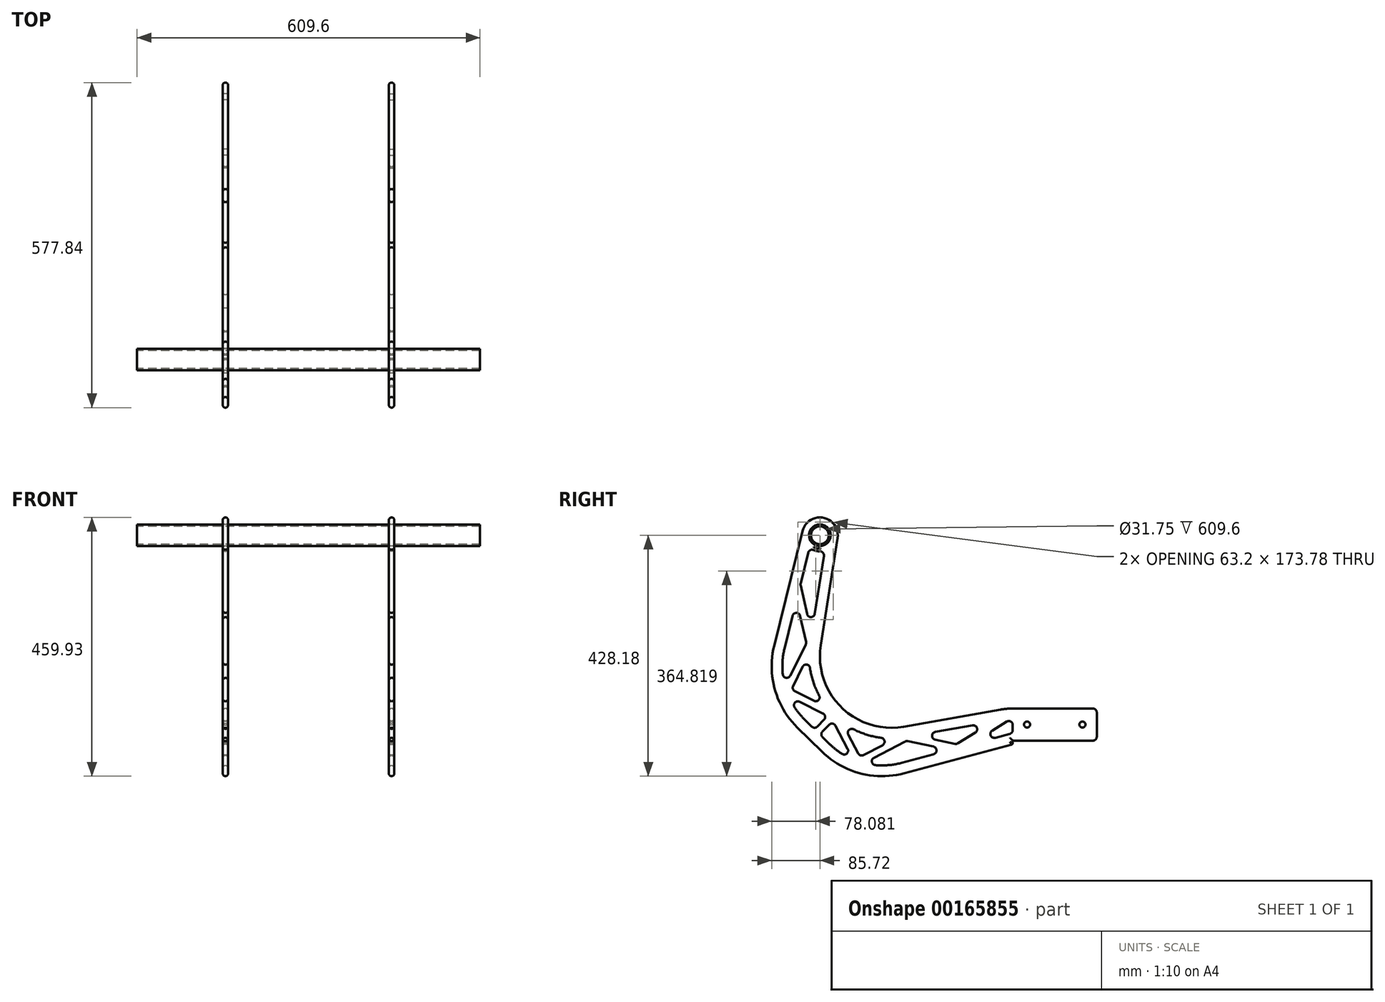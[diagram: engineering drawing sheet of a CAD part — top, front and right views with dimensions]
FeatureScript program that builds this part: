
annotation { "Feature Type Name" : "Feature", "Feature Type Description" : "" }
export const myFeature = defineFeature(function(context is Context, id is Id, definition is map)
    precondition{}
    {
        {
            var Q0;
            Q0=qCreatedBy(makeId("Right.planeOp"),FACE);
            var sketch = newSketch(context, id + "F0", { "sketchPlane" : qUnion([Q0])});
            skLineSegment(sketch, "E0", {"start": v(0, 0) * mm, "end": v(0, -228.6) * mm, "construction": true});
            skLineSegment(sketch, "E1", {"start": v(0, 0) * mm, "end": v(-279.4, 0) * mm, "construction": true});
            skLineSegment(sketch, "E2.bottom", {"start": v(0, 0) * mm, "end": v(149.23, 0) * mm, "construction": true});
            skLineSegment(sketch, "E2.top", {"start": v(0, -3.18) * mm, "end": v(149.23, -3.18) * mm, "construction": true});
            skLineSegment(sketch, "E2.left", {"start": v(0, 0) * mm, "end": v(0, -3.18) * mm, "construction": true});
            skLineSegment(sketch, "E2.right", {"start": v(149.23, 0) * mm, "end": v(149.23, -3.18) * mm, "construction": true});
            skLineSegment(sketch, "E3", {"start": v(-279.4, 0) * mm, "end": v(-279.4, 31.75) * mm, "construction": true});
            skLineSegment(sketch, "E4", {"start": v(-254, 57.15) * mm, "end": v(149.23, 57.15) * mm, "construction": true});
            skLineSegment(sketch, "E5", {"start": v(149.23, 57.15) * mm, "end": v(149.23, 0) * mm, "construction": true});
            skPoint(sketch, "E6.visualSharp", {"position": v(-279.4, 57.15) * mm});
            skArc(sketch, "E6.filletArc", {"start": v(-254, 57.15) * mm, "mid": v(-271.96, 49.71) * mm, "end": v(-279.4, 31.75) * mm, "construction": true});
            skLineSegment(sketch, "E7", {"start": v(-342.9, 0) * mm, "end": v(-342.9, 304.8) * mm, "construction": true});
            skLineSegment(sketch, "E8", {"start": v(-342.9, 0) * mm, "end": v(-279.4, 0) * mm, "construction": true});
            skSolve(sketch);
        }
        {
            var Q0;
            Q0=qCreatedBy(makeId("Right.planeOp"),FACE);
            var sketch = newSketch(context, id + "F1", { "sketchPlane" : qUnion([Q0])});
            skCircle(sketch, "E9", {"center": v(-342.9, 304.8) * mm, "radius": 19.05 * mm});
            skCircle(sketch, "E10", {"center": v(-342.9, 304.8) * mm, "radius": 15.88 * mm});
            skSolve(sketch);
        }
        {
            var Q0;
            Q0 = qSketchRegion(id + "F1", true);
            extrude(context, id + "F2", {"entities" : qUnion([Q0]), "endBound" : BoundingType.SYMMETRIC, "depth" : 609.6 * mm});
        }
        {
            var Q0;
            Q0=qCreatedBy(makeId("Right.planeOp"),FACE);
            cPlane(context, id + "F3", {"entities" : qUnion([Q0]), "cplaneType" : CPlaneType.OFFSET, "offset" : 152.4 * mm, "width" : 152.4 * mm, "height" : 152.4 * mm});
        }
        {
            var Q0;
            Q0=qCreatedBy(id+"F3.planeOp",FACE);
            var sketch = newSketch(context, id + "F4", { "sketchPlane" : qUnion([Q0])});
            skLineSegment(sketch, "E11.0", {"start": v(0, -3.18) * mm, "end": v(149.23, -3.18) * mm});
            skCircle(sketch, "E12", {"center": v(-342.9, 304.8) * mm, "radius": 19.24 * mm});
            skCircle(sketch, "E13", {"center": v(-342.9, 304.8) * mm, "radius": 31.75 * mm, "construction": true});
            skArc(sketch, "E14", {"start": v(-311.53, 299.89) * mm, "mid": v(-336.62, 335.92) * mm, "end": v(-373.72, 312.43) * mm});
            skLineSegment(sketch, "E15", {"start": v(-22.05, -5.1) * mm, "end": v(-193.85, -35.4) * mm});
            skLineSegment(sketch, "E16", {"start": v(-341.37, 109.32) * mm, "end": v(-311.53, 299.89) * mm});
            skLineSegment(sketch, "E17", {"start": v(-373.72, 312.43) * mm, "end": v(-424.16, 108.6) * mm});
            skLineSegment(sketch, "E18", {"start": v(-382.94, -36.8) * mm, "end": v(-339.15, -79.77) * mm});
            skLineSegment(sketch, "E19", {"start": v(-192.98, -118.18) * mm, "end": v(0, -66.47) * mm});
            skLineSegment(sketch, "E20", {"start": v(0, -60.33) * mm, "end": v(149.23, -60.33) * mm});
            skLineSegment(sketch, "E21", {"start": v(149.23, -60.33) * mm, "end": v(149.23, -3.18) * mm});
            skArc(sketch, "E22", {"start": v(-341.37, 109.32) * mm, "mid": v(-304.84, -0.99) * mm, "end": v(-193.85, -35.4) * mm});
            skArc(sketch, "E23", {"start": v(0, -3.18) * mm, "mid": v(-11.07, -3.66) * mm, "end": v(-22.05, -5.1) * mm});
            skLineSegment(sketch, "E24", {"start": v(-422.67, 114.6) * mm, "end": v(-187, -116.58) * mm, "construction": true});
            skLineSegment(sketch, "E25", {"start": v(-361.05, -58.29) * mm, "end": v(-304.84, -0.99) * mm, "construction": true});
            skLineSegment(sketch, "E26", {"start": v(-420.05, 125.18) * mm, "end": v(-381.06, 115.53) * mm, "construction": true});
            skLineSegment(sketch, "E27", {"start": v(-381.06, 115.53) * mm, "end": v(-341.37, 109.32) * mm, "construction": true});
            skLineSegment(sketch, "E28", {"start": v(-420.05, 125.18) * mm, "end": v(-341.37, 109.32) * mm, "construction": true});
            skPoint(sketch, "E29.visualSharp", {"position": v(22.95, -60.33) * mm});
            skPoint(sketch, "E30.visualSharp", {"position": v(-277.03, -140.7) * mm});
            skArc(sketch, "E30.filletArc", {"start": v(-339.15, -79.77) * mm, "mid": v(-271.16, -118.37) * mm, "end": v(-192.98, -118.18) * mm});
            skPoint(sketch, "E31.visualSharp", {"position": v(-445.06, 24.13) * mm});
            skArc(sketch, "E31.filletArc", {"start": v(-424.16, 108.6) * mm, "mid": v(-422.85, 30.43) * mm, "end": v(-382.94, -36.8) * mm});
            skLineSegment(sketch, "E32", {"start": v(0, -60.33) * mm, "end": v(0, -66.47) * mm});
            skSolve(sketch);
        }
        {
            var Q0;
            Q0 = qSketchRegion(id + "F4", true);
            extrude(context, id + "F5", {"entities" : qUnion([Q0]), "oppositeDirection" : true, "depth" : 9.52 * mm});
        }
        {
            var Q0;
            Q0=makeQuery(id+"F5.opExtrude","CAP_FACE",FACE,{"disambiguationData":[OSD([sQuery(id+"F4.wireOp",EDGE,"E11.0"),sQuery(id+"F4.wireOp",EDGE,"E12"),sQuery(id+"F4.wireOp",EDGE,"E14"),sQuery(id+"F4.wireOp",EDGE,"E15"),sQuery(id+"F4.wireOp",EDGE,"E16"),sQuery(id+"F4.wireOp",EDGE,"E17"),sQuery(id+"F4.wireOp",EDGE,"E18"),sQuery(id+"F4.wireOp",EDGE,"E19"),sQuery(id+"F4.wireOp",EDGE,"E20"),sQuery(id+"F4.wireOp",EDGE,"E21"),sQuery(id+"F4.wireOp",EDGE,"E22"),sQuery(id+"F4.wireOp",EDGE,"E23"),sQuery(id+"F4.wireOp",EDGE,"E29.filletArc"),sQuery(id+"F4.wireOp",EDGE,"E30.filletArc"),sQuery(id+"F4.wireOp",EDGE,"E31.filletArc")])],"isStart":true});
            var sketch = newSketch(context, id + "F6", { "sketchPlane" : qUnion([Q0])});
            skArc(sketch, "E33.0", {"start": v(-330.35, 302.84) * mm, "mid": v(-340.39, 317.25) * mm, "end": v(-355.23, 307.85) * mm, "construction": true});
            skLineSegment(sketch, "E33.1", {"start": v(-357.55, 129.11) * mm, "end": v(-335.84, 267.8) * mm});
            skArc(sketch, "E33.2", {"start": v(-361.87, 94.52) * mm, "mid": v(-354.52, 43.68) * mm, "end": v(-330.02, -1.47) * mm});
            skLineSegment(sketch, "E33.5", {"start": v(-369.6, -23.2) * mm, "end": v(-352.24, -40.24) * mm});
            skArc(sketch, "E33.6", {"start": v(-405.67, 104.02) * mm, "mid": v(-409.56, 70.29) * mm, "end": v(-404.8, 36.66) * mm});
            skLineSegment(sketch, "E33.10", {"start": v(-355.23, 307.85) * mm, "end": v(-359.6, 290.15) * mm, "construction": true});
            skLineSegment(sketch, "E34", {"start": v(-347.7, -44.69) * mm, "end": v(-318.18, -14.59) * mm, "construction": true});
            skArc(sketch, "E35", {"start": v(-333.17, 284.82) * mm, "mid": v(-347.3, 283.01) * mm, "end": v(-359.6, 290.15) * mm, "construction": true});
            skLineSegment(sketch, "E36", {"start": v(-333.17, 284.82) * mm, "end": v(-380.97, 203.83) * mm, "construction": true});
            skLineSegment(sketch, "E37", {"start": v(-380.97, 203.83) * mm, "end": v(-360.22, 112.1) * mm, "construction": true});
            skLineSegment(sketch, "E38", {"start": v(-360.22, 112.1) * mm, "end": v(-402.07, 27.9) * mm, "construction": true});
            skLineSegment(sketch, "E39", {"start": v(-402.07, 27.9) * mm, "end": v(-318.18, -14.59) * mm, "construction": true});
            skLineSegment(sketch, "E40.0", {"start": v(-352.24, -40.24) * mm, "end": v(-328.78, -16.33) * mm});
            skLineSegment(sketch, "E40.1", {"start": v(-398.6, 19.02) * mm, "end": v(-328.78, -16.33) * mm});
            skArc(sketch, "E40.2", {"start": v(-345.55, 276.35) * mm, "mid": v(-353.97, 278.46) * mm, "end": v(-361.38, 283) * mm});
            skLineSegment(sketch, "E40.3", {"start": v(-345.55, 276.35) * mm, "end": v(-375.64, 225.34) * mm});
            skLineSegment(sketch, "E40.4", {"start": v(-384.37, 190.09) * mm, "end": v(-366.9, 112.91) * mm});
            skLineSegment(sketch, "E40.5", {"start": v(-366.9, 112.91) * mm, "end": v(-404.8, 36.66) * mm});
            skLineSegment(sketch, "E41.0", {"start": v(-393.58, 30.72) * mm, "end": v(-330.02, -1.47) * mm});
            skLineSegment(sketch, "E41.1", {"start": v(-361.87, 94.52) * mm, "end": v(-393.58, 30.72) * mm});
            skLineSegment(sketch, "E41.2", {"start": v(-374.22, 202.77) * mm, "end": v(-357.55, 129.11) * mm});
            skLineSegment(sketch, "E41.3", {"start": v(-335.84, 267.8) * mm, "end": v(-374.22, 202.77) * mm});
            skLineSegment(sketch, "E42.trimOffspring", {"start": v(-333.17, 284.82) * mm, "end": v(-330.35, 302.84) * mm, "construction": true});
            skArc(sketch, "E43.trimOffspring", {"start": v(-398.6, 19.02) * mm, "mid": v(-386.15, -3.5) * mm, "end": v(-369.6, -23.2) * mm});
            skLineSegment(sketch, "E44", {"start": v(-361.05, -58.29) * mm, "end": v(-347.7, -44.69) * mm, "construction": true});
            skLineSegment(sketch, "E45.trimOffspring", {"start": v(-384.37, 190.09) * mm, "end": v(-405.67, 104.02) * mm});
            skLineSegment(sketch, "E46.trimOffspring", {"start": v(-361.38, 283) * mm, "end": v(-375.64, 225.34) * mm});
            skArc(sketch, "E47.MirrorCS", {"start": v(-26.77, -36.36) * mm, "mid": v(-24.5, -44.75) * mm, "end": v(-19.81, -52.06) * mm});
            skArc(sketch, "E48.MirrorCS", {"start": v(-197.9, -99.78) * mm, "mid": v(-231.56, -104.32) * mm, "end": v(-265.27, -100.22) * mm});
            skLineSegment(sketch, "E49.MirrorCS", {"start": v(-271.43, -89.1) * mm, "end": v(-304.84, -26.17) * mm});
            skArc(sketch, "E50.MirrorCS", {"start": v(-18.54, -23.83) * mm, "mid": v(-20.07, -37.98) * mm, "end": v(-12.7, -50.16) * mm, "construction": true});
            skLineSegment(sketch, "E51.MirrorCS", {"start": v(-112.27, -76.84) * mm, "end": v(-197.9, -99.78) * mm});
            skLineSegment(sketch, "E52.MirrorCS", {"start": v(-173.75, -51.2) * mm, "end": v(-35.5, -26.82) * mm});
            skLineSegment(sketch, "E53.MirrorCS", {"start": v(-189.77, -60.86) * mm, "end": v(-265.27, -100.22) * mm});
            skLineSegment(sketch, "E54.MirrorCS", {"start": v(-19.81, -52.06) * mm, "end": v(-77.19, -67.43) * mm});
            skLineSegment(sketch, "E55.MirrorCS", {"start": v(-26.77, -36.36) * mm, "end": v(-77.19, -67.43) * mm});
            skLineSegment(sketch, "E56.MirrorCS", {"start": v(-35.5, -26.82) * mm, "end": v(-99.78, -66.44) * mm});
            skLineSegment(sketch, "E57.MirrorCS", {"start": v(-208.26, -56.18) * mm, "end": v(-271.43, -89.1) * mm});
            skLineSegment(sketch, "E58.MirrorCS", {"start": v(-274.09, -97.65) * mm, "end": v(-318.18, -14.59) * mm, "construction": true});
            skArc(sketch, "E59.MirrorCS", {"start": v(-208.26, -56.18) * mm, "mid": v(-259.23, -49.8) * mm, "end": v(-304.84, -26.17) * mm});
            skArc(sketch, "E60.MirrorCS", {"start": v(-283.03, -94.35) * mm, "mid": v(-305.78, -82.33) * mm, "end": v(-325.8, -66.17) * mm});
            skLineSegment(sketch, "E61.MirrorCS", {"start": v(-18.54, -23.83) * mm, "end": v(-98.6, -73.17) * mm, "construction": true});
            skLineSegment(sketch, "E62.MirrorCS", {"start": v(-112.27, -76.84) * mm, "end": v(-189.77, -60.86) * mm});
            skLineSegment(sketch, "E63.MirrorCS", {"start": v(-190.7, -54.18) * mm, "end": v(-274.09, -97.65) * mm, "construction": true});
            skLineSegment(sketch, "E64.MirrorCS", {"start": v(-98.6, -73.17) * mm, "end": v(-190.7, -54.18) * mm, "construction": true});
            skLineSegment(sketch, "E65.MirrorCS", {"start": v(-343.17, -49.13) * mm, "end": v(-319.72, -25.23) * mm});
            skLineSegment(sketch, "E66.MirrorCS", {"start": v(-283.03, -94.35) * mm, "end": v(-319.72, -25.23) * mm});
            skLineSegment(sketch, "E67.MirrorCS", {"start": v(-99.78, -66.44) * mm, "end": v(-173.75, -51.2) * mm});
            skLineSegment(sketch, "E68.MirrorCS", {"start": v(-325.8, -66.17) * mm, "end": v(-343.17, -49.13) * mm});
            skLineSegment(sketch, "E69.MirrorCS", {"start": v(4.91, -45.44) * mm, "end": v(-12.7, -50.16) * mm, "construction": true});
            skArc(sketch, "E70.MirrorCS", {"start": v(-0.58, -20.66) * mm, "mid": v(14.02, -30.42) * mm, "end": v(4.91, -45.44) * mm, "construction": true});
            skLineSegment(sketch, "E71.MirrorCS", {"start": v(-18.54, -23.83) * mm, "end": v(-0.58, -20.66) * mm, "construction": true});
            skSolve(sketch);
        }
        {
            var Q0;
            Q0 = qSketchRegion(id + "F6", true);
            extrude(context, id + "F7", {"entities" : qUnion([Q0]), "operationType" : NewBodyOperationType.REMOVE, "oppositeDirection" : true, "depth" : 25.4 * mm});
        }
        {
            var Q0;
            Q0=makeQuery(id+"F5.opExtrude","CAP_FACE",FACE,{"disambiguationData":[OSD([sQuery(id+"F4.wireOp",EDGE,"E11.0"),sQuery(id+"F4.wireOp",EDGE,"E12"),sQuery(id+"F4.wireOp",EDGE,"E14"),sQuery(id+"F4.wireOp",EDGE,"E15"),sQuery(id+"F4.wireOp",EDGE,"E16"),sQuery(id+"F4.wireOp",EDGE,"E17"),sQuery(id+"F4.wireOp",EDGE,"E18"),sQuery(id+"F4.wireOp",EDGE,"E19"),sQuery(id+"F4.wireOp",EDGE,"E20"),sQuery(id+"F4.wireOp",EDGE,"E21"),sQuery(id+"F4.wireOp",EDGE,"E22"),sQuery(id+"F4.wireOp",EDGE,"E23"),sQuery(id+"F4.wireOp",EDGE,"E29.filletArc"),sQuery(id+"F4.wireOp",EDGE,"E30.filletArc"),sQuery(id+"F4.wireOp",EDGE,"E31.filletArc")])],"isStart":true});
            var sketch = newSketch(context, id + "F8", { "sketchPlane" : qUnion([Q0])});
            skLineSegment(sketch, "E72", {"start": v(-377.57, 217.57) * mm, "end": v(-361.38, 283) * mm});
            skArc(sketch, "E73", {"start": v(-361.38, 283) * mm, "mid": v(-348.55, 276.79) * mm, "end": v(-334.31, 277.55) * mm});
            skLineSegment(sketch, "E74", {"start": v(-334.31, 277.55) * mm, "end": v(-357.55, 129.11) * mm});
            skLineSegment(sketch, "E75", {"start": v(-357.55, 129.11) * mm, "end": v(-377.57, 217.57) * mm});
            skLineSegment(sketch, "E76", {"start": v(-77.19, -67.43) * mm, "end": v(0, -19.86) * mm});
            skLineSegment(sketch, "E77", {"start": v(0, -46.75) * mm, "end": v(-77.19, -67.43) * mm});
            skLineSegment(sketch, "E78", {"start": v(0, -19.86) * mm, "end": v(0, -46.75) * mm});
            skSolve(sketch);
        }
        {
            var Q0;
            Q0 = qSketchRegion(id + "F8", true);
            extrude(context, id + "F9", {"entities" : qUnion([Q0]), "operationType" : NewBodyOperationType.REMOVE, "oppositeDirection" : true, "depth" : 25.4 * mm});
        }
        {
            var Q0;
            Q0=makeQuery(id+"F7.boolean.opBoolean","COPY",EDGE,{"derivedFrom":makeQuery(id+"F7.opExtrude","SWEPT_EDGE",EDGE,{"disambiguationData":[OSD([sQuery(id+"F6.wireOp",EDGE,"E33.5"),sQuery(id+"F6.wireOp",EDGE,"E40.0")])]})});
            var Q1;
            Q1=makeQuery(id+"F7.boolean.opBoolean","COPY",EDGE,{"derivedFrom":makeQuery(id+"F7.opExtrude","SWEPT_EDGE",EDGE,{"disambiguationData":[OSD([sQuery(id+"F6.wireOp",EDGE,"E40.0"),sQuery(id+"F6.wireOp",EDGE,"E40.1")])]})});
            var Q2;
            Q2=makeQuery(id+"F7.boolean.opBoolean","COPY",EDGE,{"derivedFrom":makeQuery(id+"F7.opExtrude","SWEPT_EDGE",EDGE,{"disambiguationData":[OSD([sQuery(id+"F6.wireOp",EDGE,"E40.1"),sQuery(id+"F6.wireOp",EDGE,"E43.trimOffspring")])]})});
            var Q3;
            Q3=makeQuery(id+"F7.boolean.opBoolean","COPY",EDGE,{"derivedFrom":makeQuery(id+"F7.opExtrude","SWEPT_EDGE",EDGE,{"disambiguationData":[OSD([sQuery(id+"F6.wireOp",EDGE,"E41.0"),sQuery(id+"F6.wireOp",EDGE,"E41.1")])]})});
            var Q4;
            Q4=makeQuery(id+"F7.boolean.opBoolean","COPY",EDGE,{"derivedFrom":makeQuery(id+"F7.opExtrude","SWEPT_EDGE",EDGE,{"disambiguationData":[OSD([sQuery(id+"F6.wireOp",EDGE,"E33.2"),sQuery(id+"F6.wireOp",EDGE,"E41.0")])]})});
            var Q5;
            Q5=makeQuery(id+"F7.boolean.opBoolean","COPY",EDGE,{"derivedFrom":makeQuery(id+"F7.opExtrude","SWEPT_EDGE",EDGE,{"disambiguationData":[OSD([sQuery(id+"F6.wireOp",EDGE,"E33.2"),sQuery(id+"F6.wireOp",EDGE,"E41.1")])]})});
            var Q6;
            Q6=makeQuery(id+"F7.boolean.opBoolean","COPY",EDGE,{"derivedFrom":makeQuery(id+"F7.opExtrude","SWEPT_EDGE",EDGE,{"disambiguationData":[OSD([sQuery(id+"F6.wireOp",EDGE,"E33.6"),sQuery(id+"F6.wireOp",EDGE,"E40.5")])]})});
            var Q7;
            Q7=makeQuery(id+"F7.boolean.opBoolean","COPY",EDGE,{"derivedFrom":makeQuery(id+"F7.opExtrude","SWEPT_EDGE",EDGE,{"disambiguationData":[OSD([sQuery(id+"F6.wireOp",EDGE,"E40.4"),sQuery(id+"F6.wireOp",EDGE,"E40.5")])]})});
            var Q8;
            Q8=makeQuery(id+"F7.boolean.opBoolean","COPY",EDGE,{"derivedFrom":makeQuery(id+"F7.opExtrude","SWEPT_EDGE",EDGE,{"disambiguationData":[OSD([sQuery(id+"F6.wireOp",EDGE,"E40.4"),sQuery(id+"F6.wireOp",EDGE,"E45.trimOffspring")])]})});
            var Q9;
            Q9=makeQuery(id+"F7.boolean.opBoolean","COPY",EDGE,{"derivedFrom":makeQuery(id+"F7.opExtrude","SWEPT_EDGE",EDGE,{"disambiguationData":[OSD([sQuery(id+"F6.wireOp",EDGE,"E41.2"),sQuery(id+"F6.wireOp",EDGE,"E41.3")])]})});
            var Q10;
            Q10=makeQuery(id+"F7.boolean.opBoolean","COPY",EDGE,{"derivedFrom":makeQuery(id+"F7.opExtrude","SWEPT_EDGE",EDGE,{"disambiguationData":[OSD([sQuery(id+"F6.wireOp",EDGE,"E33.1"),sQuery(id+"F6.wireOp",EDGE,"E41.3")])]})});
            var Q11;
            Q11=makeQuery(id+"F7.boolean.opBoolean","COPY",EDGE,{"derivedFrom":makeQuery(id+"F7.opExtrude","SWEPT_EDGE",EDGE,{"disambiguationData":[OSD([sQuery(id+"F6.wireOp",EDGE,"E33.1"),sQuery(id+"F6.wireOp",EDGE,"E41.2")])]})});
            var Q12;
            Q12=makeQuery(id+"F9.boolean.opBoolean","COPY",EDGE,{"derivedFrom":makeQuery(id+"F9.opExtrude","SWEPT_EDGE",EDGE,{"disambiguationData":[OSD([sQuery(id+"F8.wireOp",EDGE,"E72"),sQuery(id+"F8.wireOp",EDGE,"E75")])]})});
            var Q13;
            Q13=makeQuery(id+"F7.boolean.opBoolean","COPY",EDGE,{"derivedFrom":makeQuery(id+"F7.opExtrude","SWEPT_EDGE",EDGE,{"disambiguationData":[OSD([sQuery(id+"F6.wireOp",EDGE,"E40.2"),sQuery(id+"F6.wireOp",EDGE,"E46.trimOffspring")])]})});
            var Q14;
            Q14=makeQuery(id+"F9.boolean.opBoolean","COPY",EDGE,{"derivedFrom":makeQuery(id+"F9.opExtrude","SWEPT_EDGE",EDGE,{"disambiguationData":[OSD([sQuery(id+"F8.wireOp",EDGE,"E73"),sQuery(id+"F8.wireOp",EDGE,"E74")])]})});
            var Q15;
            Q15=makeQuery(id+"F7.boolean.opBoolean","COPY",EDGE,{"derivedFrom":makeQuery(id+"F7.opExtrude","SWEPT_EDGE",EDGE,{"disambiguationData":[OSD([sQuery(id+"F6.wireOp",EDGE,"E65.MirrorCS"),sQuery(id+"F6.wireOp",EDGE,"E68.MirrorCS")])]})});
            var Q16;
            Q16=makeQuery(id+"F7.boolean.opBoolean","COPY",EDGE,{"derivedFrom":makeQuery(id+"F7.opExtrude","SWEPT_EDGE",EDGE,{"disambiguationData":[OSD([sQuery(id+"F6.wireOp",EDGE,"E65.MirrorCS"),sQuery(id+"F6.wireOp",EDGE,"E66.MirrorCS")])]})});
            var Q17;
            Q17=makeQuery(id+"F7.boolean.opBoolean","COPY",EDGE,{"derivedFrom":makeQuery(id+"F7.opExtrude","SWEPT_EDGE",EDGE,{"disambiguationData":[OSD([sQuery(id+"F6.wireOp",EDGE,"E60.MirrorCS"),sQuery(id+"F6.wireOp",EDGE,"E66.MirrorCS")])]})});
            var Q18;
            Q18=makeQuery(id+"F7.boolean.opBoolean","COPY",EDGE,{"derivedFrom":makeQuery(id+"F7.opExtrude","SWEPT_EDGE",EDGE,{"disambiguationData":[OSD([sQuery(id+"F6.wireOp",EDGE,"E49.MirrorCS"),sQuery(id+"F6.wireOp",EDGE,"E57.MirrorCS")])]})});
            var Q19;
            Q19=makeQuery(id+"F7.boolean.opBoolean","COPY",EDGE,{"derivedFrom":makeQuery(id+"F7.opExtrude","SWEPT_EDGE",EDGE,{"disambiguationData":[OSD([sQuery(id+"F6.wireOp",EDGE,"E49.MirrorCS"),sQuery(id+"F6.wireOp",EDGE,"E59.MirrorCS")])]})});
            var Q20;
            Q20=makeQuery(id+"F7.boolean.opBoolean","COPY",EDGE,{"derivedFrom":makeQuery(id+"F7.opExtrude","SWEPT_EDGE",EDGE,{"disambiguationData":[OSD([sQuery(id+"F6.wireOp",EDGE,"E57.MirrorCS"),sQuery(id+"F6.wireOp",EDGE,"E59.MirrorCS")])]})});
            var Q21;
            Q21=makeQuery(id+"F7.boolean.opBoolean","COPY",EDGE,{"derivedFrom":makeQuery(id+"F7.opExtrude","SWEPT_EDGE",EDGE,{"disambiguationData":[OSD([sQuery(id+"F6.wireOp",EDGE,"E53.MirrorCS"),sQuery(id+"F6.wireOp",EDGE,"E62.MirrorCS")])]})});
            var Q22;
            Q22=makeQuery(id+"F7.boolean.opBoolean","COPY",EDGE,{"derivedFrom":makeQuery(id+"F7.opExtrude","SWEPT_EDGE",EDGE,{"disambiguationData":[OSD([sQuery(id+"F6.wireOp",EDGE,"E48.MirrorCS"),sQuery(id+"F6.wireOp",EDGE,"E53.MirrorCS")])]})});
            var Q23;
            Q23=makeQuery(id+"F7.boolean.opBoolean","COPY",EDGE,{"derivedFrom":makeQuery(id+"F7.opExtrude","SWEPT_EDGE",EDGE,{"disambiguationData":[OSD([sQuery(id+"F6.wireOp",EDGE,"E51.MirrorCS"),sQuery(id+"F6.wireOp",EDGE,"E62.MirrorCS")])]})});
            var Q24;
            Q24=makeQuery(id+"F7.boolean.opBoolean","COPY",EDGE,{"derivedFrom":makeQuery(id+"F7.opExtrude","SWEPT_EDGE",EDGE,{"disambiguationData":[OSD([sQuery(id+"F6.wireOp",EDGE,"E52.MirrorCS"),sQuery(id+"F6.wireOp",EDGE,"E67.MirrorCS")])]})});
            var Q25;
            Q25=makeQuery(id+"F7.boolean.opBoolean","COPY",EDGE,{"derivedFrom":makeQuery(id+"F7.opExtrude","SWEPT_EDGE",EDGE,{"disambiguationData":[OSD([sQuery(id+"F6.wireOp",EDGE,"E56.MirrorCS"),sQuery(id+"F6.wireOp",EDGE,"E67.MirrorCS")])]})});
            var Q26;
            Q26=makeQuery(id+"F7.boolean.opBoolean","COPY",EDGE,{"derivedFrom":makeQuery(id+"F7.opExtrude","SWEPT_EDGE",EDGE,{"disambiguationData":[OSD([sQuery(id+"F6.wireOp",EDGE,"E54.MirrorCS"),sQuery(id+"F6.wireOp",EDGE,"E55.MirrorCS")])]})});
            var Q27;
            Q27=makeQuery(id+"F7.boolean.opBoolean","COPY",EDGE,{"derivedFrom":makeQuery(id+"F7.opExtrude","SWEPT_EDGE",EDGE,{"disambiguationData":[OSD([sQuery(id+"F6.wireOp",EDGE,"E52.MirrorCS"),sQuery(id+"F6.wireOp",EDGE,"E56.MirrorCS")])]})});
            var Q28;
            Q28=makeQuery(id+"F9.boolean.opBoolean","COPY",EDGE,{"derivedFrom":makeQuery(id+"F9.opExtrude","SWEPT_EDGE",EDGE,{"disambiguationData":[OSD([sQuery(id+"F8.wireOp",EDGE,"E76"),sQuery(id+"F8.wireOp",EDGE,"QhLc7K4z-Akcm-oFJL-4TFC-ttLu0XXbbSw1")])]})});
            var Q29;
            Q29=makeQuery(id+"F9.boolean.opBoolean","COPY",EDGE,{"derivedFrom":makeQuery(id+"F9.opExtrude","SWEPT_EDGE",EDGE,{"disambiguationData":[OSD([sQuery(id+"F8.wireOp",EDGE,"QhLc7K4z-Akcm-oFJL-4TFC-ttLu0XXbbSw1"),sQuery(id+"F8.wireOp",EDGE,"bKYI4NnU-ni6z-fiqR-xN9G-CCJAb1qPsRIM")])]})});
            var Q30;
            Q30=makeQuery(id+"F9.boolean.opBoolean","COPY",EDGE,{"derivedFrom":makeQuery(id+"F9.opExtrude","SWEPT_EDGE",EDGE,{"disambiguationData":[OSD([sQuery(id+"F8.wireOp",EDGE,"bKYI4NnU-ni6z-fiqR-xN9G-CCJAb1qPsRIM"),sQuery(id+"F8.wireOp",EDGE,"E77")])]})});
            var Q31;
            Q31=makeQuery(id+"F5.opExtrude","SWEPT_EDGE",EDGE,{"disambiguationData":[OSD([sQuery(id+"F4.wireOp",EDGE,"E11.0"),sQuery(id+"F4.wireOp",EDGE,"E21")])]});
            var Q32;
            Q32=makeQuery(id+"F5.opExtrude","SWEPT_EDGE",EDGE,{"disambiguationData":[OSD([sQuery(id+"F4.wireOp",EDGE,"E20"),sQuery(id+"F4.wireOp",EDGE,"E21")])]});
            fillet(context, id + "F10", {"entities" : qUnion([Q0, Q1, Q2, Q3, Q4, Q5, Q6, Q7, Q8, Q9, Q10, Q11, Q12, Q13, Q14, Q15, Q16, Q17, Q18, Q19, Q20, Q21, Q22, Q23, Q24, Q25, Q26, Q27, Q28, Q29, Q30, Q31, Q32]), "radius" : 7 * mm, "tangentPropagation" : true, "allowEdgeOverflow" : false});
        }
        {
            var Q0;
            Q0=makeQuery(id+"F5.opExtrude","SWEPT_EDGE",EDGE,{"disambiguationData":[OSD([sQuery(id+"F4.wireOp",EDGE,"E19"),sQuery(id+"F4.wireOp",EDGE,"E32")])]});
            fillet(context, id + "F11", {"entities" : qUnion([Q0]), "radius" : 3.17 * mm, "tangentPropagation" : true, "allowEdgeOverflow" : false});
        }
        {
            var Q0;
            Q0=makeQuery(id+"F5.opExtrude","CAP_FACE",FACE,{"disambiguationData":[OSD([sQuery(id+"F4.wireOp",EDGE,"E11.0"),sQuery(id+"F4.wireOp",EDGE,"E12"),sQuery(id+"F4.wireOp",EDGE,"E14"),sQuery(id+"F4.wireOp",EDGE,"E15"),sQuery(id+"F4.wireOp",EDGE,"E16"),sQuery(id+"F4.wireOp",EDGE,"E17"),sQuery(id+"F4.wireOp",EDGE,"E18"),sQuery(id+"F4.wireOp",EDGE,"E19"),sQuery(id+"F4.wireOp",EDGE,"E20"),sQuery(id+"F4.wireOp",EDGE,"E21"),sQuery(id+"F4.wireOp",EDGE,"E22"),sQuery(id+"F4.wireOp",EDGE,"E23"),sQuery(id+"F4.wireOp",EDGE,"E30.filletArc"),sQuery(id+"F4.wireOp",EDGE,"E31.filletArc"),sQuery(id+"F4.wireOp",EDGE,"E32")])],"isStart":true});
            var sketch = newSketch(context, id + "F12", { "sketchPlane" : qUnion([Q0])});
            skLineSegment(sketch, "E79", {"start": v(149.22, -31.75) * mm, "end": v(0, -31.75) * mm, "construction": true});
            skPoint(sketch, "E79.endSnap0", {"position": v(0, -36.88) * mm});
            skLineSegment(sketch, "E80", {"start": v(74.61, -31.75) * mm, "end": v(74.61, -3.18) * mm, "construction": true});
            skPoint(sketch, "E81", {"position": v(123.83, -31.75) * mm});
            skPoint(sketch, "E82.MirrorP", {"position": v(25.4, -31.75) * mm});
            skSolve(sketch);
        }
        {
            var Q0;
            Q0=makeQuery(id+"F5.opExtrude","CAP_FACE",FACE,{"disambiguationData":[OSD([sQuery(id+"F4.wireOp",EDGE,"E11.0"),sQuery(id+"F4.wireOp",EDGE,"E12"),sQuery(id+"F4.wireOp",EDGE,"E14"),sQuery(id+"F4.wireOp",EDGE,"E15"),sQuery(id+"F4.wireOp",EDGE,"E16"),sQuery(id+"F4.wireOp",EDGE,"E17"),sQuery(id+"F4.wireOp",EDGE,"E18"),sQuery(id+"F4.wireOp",EDGE,"E19"),sQuery(id+"F4.wireOp",EDGE,"E20"),sQuery(id+"F4.wireOp",EDGE,"E21"),sQuery(id+"F4.wireOp",EDGE,"E22"),sQuery(id+"F4.wireOp",EDGE,"E23"),sQuery(id+"F4.wireOp",EDGE,"E29.filletArc"),sQuery(id+"F4.wireOp",EDGE,"E30.filletArc"),sQuery(id+"F4.wireOp",EDGE,"E31.filletArc")])],"isStart":true});
            var Q1;
            Q1=makeQuery(id+"F5.opExtrude","CAP_FACE",FACE,{"disambiguationData":[OSD([sQuery(id+"F4.wireOp",EDGE,"E11.0"),sQuery(id+"F4.wireOp",EDGE,"E12"),sQuery(id+"F4.wireOp",EDGE,"E14"),sQuery(id+"F4.wireOp",EDGE,"E15"),sQuery(id+"F4.wireOp",EDGE,"E16"),sQuery(id+"F4.wireOp",EDGE,"E17"),sQuery(id+"F4.wireOp",EDGE,"E18"),sQuery(id+"F4.wireOp",EDGE,"E19"),sQuery(id+"F4.wireOp",EDGE,"E20"),sQuery(id+"F4.wireOp",EDGE,"E21"),sQuery(id+"F4.wireOp",EDGE,"E22"),sQuery(id+"F4.wireOp",EDGE,"E23"),sQuery(id+"F4.wireOp",EDGE,"E29.filletArc"),sQuery(id+"F4.wireOp",EDGE,"E30.filletArc"),sQuery(id+"F4.wireOp",EDGE,"E31.filletArc")])],"isStart":false});
            fillet(context, id + "F13", {"entities" : qUnion([Q0, Q1]), "radius" : 4.76 * mm, "tangentPropagation" : true, "allowEdgeOverflow" : false});
        }
        {
            var Q0;
            Q0=sQuery(id+"F12.wireOp",VERTEX,"E82.MirrorP");
            var Q1;
            Q1=sQuery(id+"F12.wireOp",VERTEX,"E81");
            var Q2;
            Q2=makeQuery(id+"F5.opExtrude","SWEPT_BODY",BODY,{"disambiguationData":[OSD([sQuery(id+"F4.wireOp",EDGE,"E11.0"),sQuery(id+"F4.wireOp",EDGE,"E12"),sQuery(id+"F4.wireOp",EDGE,"E14"),sQuery(id+"F4.wireOp",EDGE,"E15"),sQuery(id+"F4.wireOp",EDGE,"E16"),sQuery(id+"F4.wireOp",EDGE,"E17"),sQuery(id+"F4.wireOp",EDGE,"E18"),sQuery(id+"F4.wireOp",EDGE,"E19"),sQuery(id+"F4.wireOp",EDGE,"E20"),sQuery(id+"F4.wireOp",EDGE,"E21"),sQuery(id+"F4.wireOp",EDGE,"E22"),sQuery(id+"F4.wireOp",EDGE,"E23"),sQuery(id+"F4.wireOp",EDGE,"E30.filletArc"),sQuery(id+"F4.wireOp",EDGE,"E31.filletArc"),sQuery(id+"F4.wireOp",EDGE,"E32")])]});
            hole(context, id + "F14", {"style" : HoleStyle.SIMPLE, "endStyle" : HoleEndStyle.THROUGH, "standardTappedOrClearance" : lookupTablePath({ "standard" : "ANSI", "engagement" : "75%", "pitch" : "13 tpi", "size" : "1/2", "type" : "Tapped" }), "standardBlindInLast" : lookupTablePath({ "standard" : "ANSI", "engagement" : "75%", "pitch" : "13 tpi", "size" : "1/2", "type" : "Tapped" }), "holeDiameter" : 10.72 * mm, "locations" : qUnion([Q0, Q1]), "scope" : qUnion([Q2]), "isTappedThrough" : true, "majorDiameter" : 12.7 * mm, "showTappedDepth" : true});
        }
        {
            var Q0;
            Q0=makeQuery(id+"F5.opExtrude","SWEPT_BODY",BODY,{"disambiguationData":[OSD([sQuery(id+"F4.wireOp",EDGE,"E11.0"),sQuery(id+"F4.wireOp",EDGE,"E12"),sQuery(id+"F4.wireOp",EDGE,"E14"),sQuery(id+"F4.wireOp",EDGE,"E15"),sQuery(id+"F4.wireOp",EDGE,"E16"),sQuery(id+"F4.wireOp",EDGE,"E17"),sQuery(id+"F4.wireOp",EDGE,"E18"),sQuery(id+"F4.wireOp",EDGE,"E19"),sQuery(id+"F4.wireOp",EDGE,"E20"),sQuery(id+"F4.wireOp",EDGE,"E21"),sQuery(id+"F4.wireOp",EDGE,"E22"),sQuery(id+"F4.wireOp",EDGE,"E23"),sQuery(id+"F4.wireOp",EDGE,"E30.filletArc"),sQuery(id+"F4.wireOp",EDGE,"E31.filletArc"),sQuery(id+"F4.wireOp",EDGE,"E32")])]});
            var Q1;
            Q1=qCreatedBy(makeId("Right.planeOp"),FACE);
            mirror(context, id + "F15", {"entities" : qUnion([Q0]), "mirrorPlane" : qUnion([Q1])});
        }
    });
